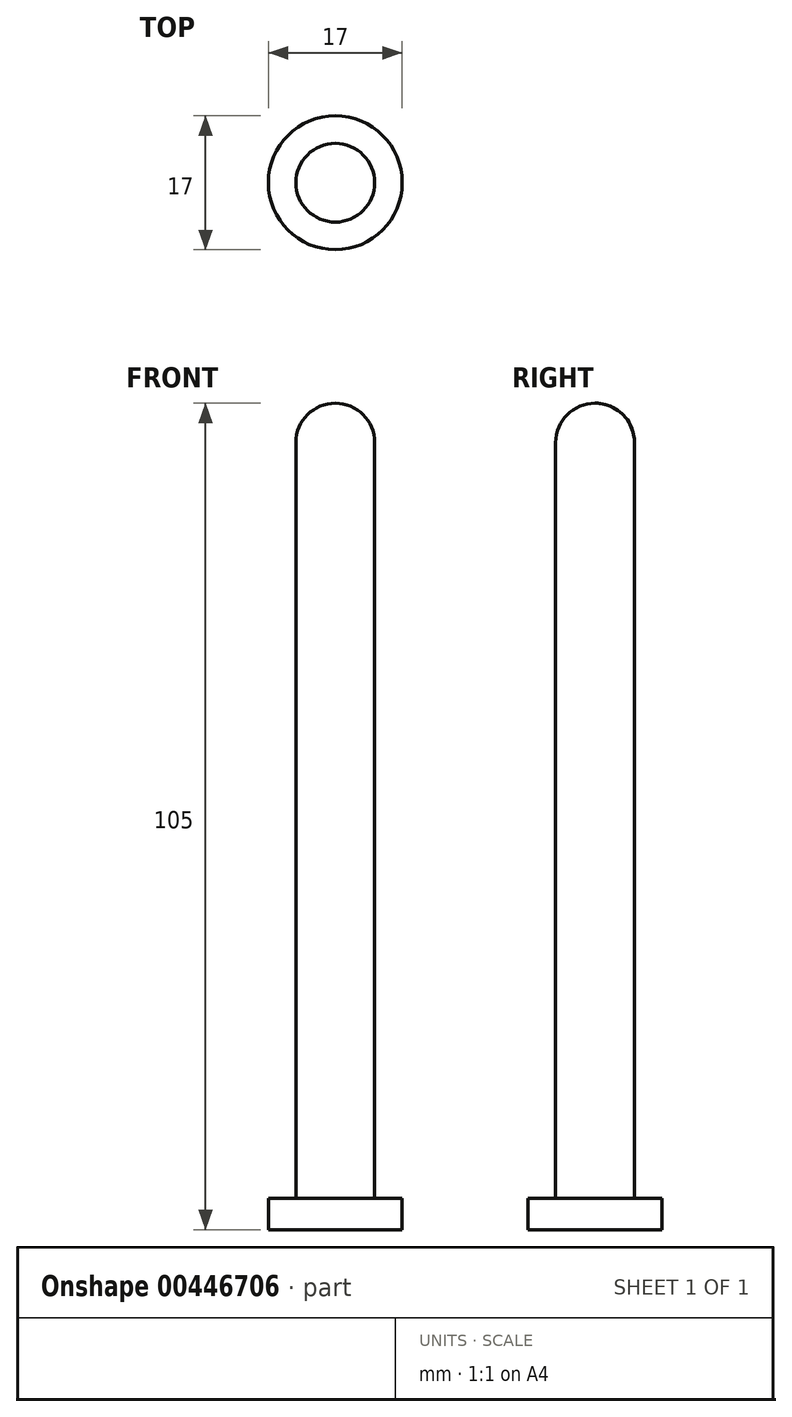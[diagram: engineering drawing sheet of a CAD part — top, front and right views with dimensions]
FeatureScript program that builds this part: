
annotation { "Feature Type Name" : "Feature", "Feature Type Description" : "" }
export const myFeature = defineFeature(function(context is Context, id is Id, definition is map)
    precondition{}
    {
        {
            var Q0;
            Q0=qCreatedBy(makeId("Top.planeOp"),FACE);
            var sketch = newSketch(context, id + "F0", { "sketchPlane" : qUnion([Q0])});
            skCircle(sketch, "E0", {"center": v(0, 0) * mm, "radius": 8.5 * mm});
            skSolve(sketch);
        }
        {
            var Q0;
            Q0=qSketchRegion(id+"F0",true);
            extrude(context, id + "F1", {"entities" : qUnion([Q0]), "depth" : 4 * mm});
        }
        {
            var Q0;
            Q0=qCreatedBy(makeId("Top.planeOp"),FACE);
            var sketch = newSketch(context, id + "F2", { "sketchPlane" : qUnion([Q0])});
            skCircle(sketch, "E1", {"center": v(0, 0) * mm, "radius": 5 * mm});
            skSolve(sketch);
        }
        {
            var Q0;
            Q0=qSketchRegion(id+"F2",true);
            extrude(context, id + "F3", {"entities" : qUnion([Q0]), "operationType" : NewBodyOperationType.ADD, "depth" : 100 * mm});
        }
        {
            var Q0;
            Q0=qCreatedBy(makeId("Right.planeOp"),FACE);
            var sketch = newSketch(context, id + "F4", { "sketchPlane" : qUnion([Q0])});
            skArc(sketch, "E2", {"start": v(5, 100) * mm, "mid": v(3.54, 103.54) * mm, "end": v(0, 105) * mm});
            skLineSegment(sketch, "E3", {"start": v(0, 105) * mm, "end": v(0, 100) * mm});
            skLineSegment(sketch, "E4", {"start": v(0, 100) * mm, "end": v(5, 100) * mm});
            skSolve(sketch);
        }
        {
            var Q0;
            Q0=qSketchRegion(id+"F4",true);
            var Q1;
            Q1=sQuery(id+"F4.wireOp",EDGE,"E3");
            revolve(context, id + "F5", {"operationType" : NewBodyOperationType.ADD, "entities" : qUnion([Q0]), "axis" : qUnion([Q1]), "revolveType" : RevolveType.FULL});
        }
    });
